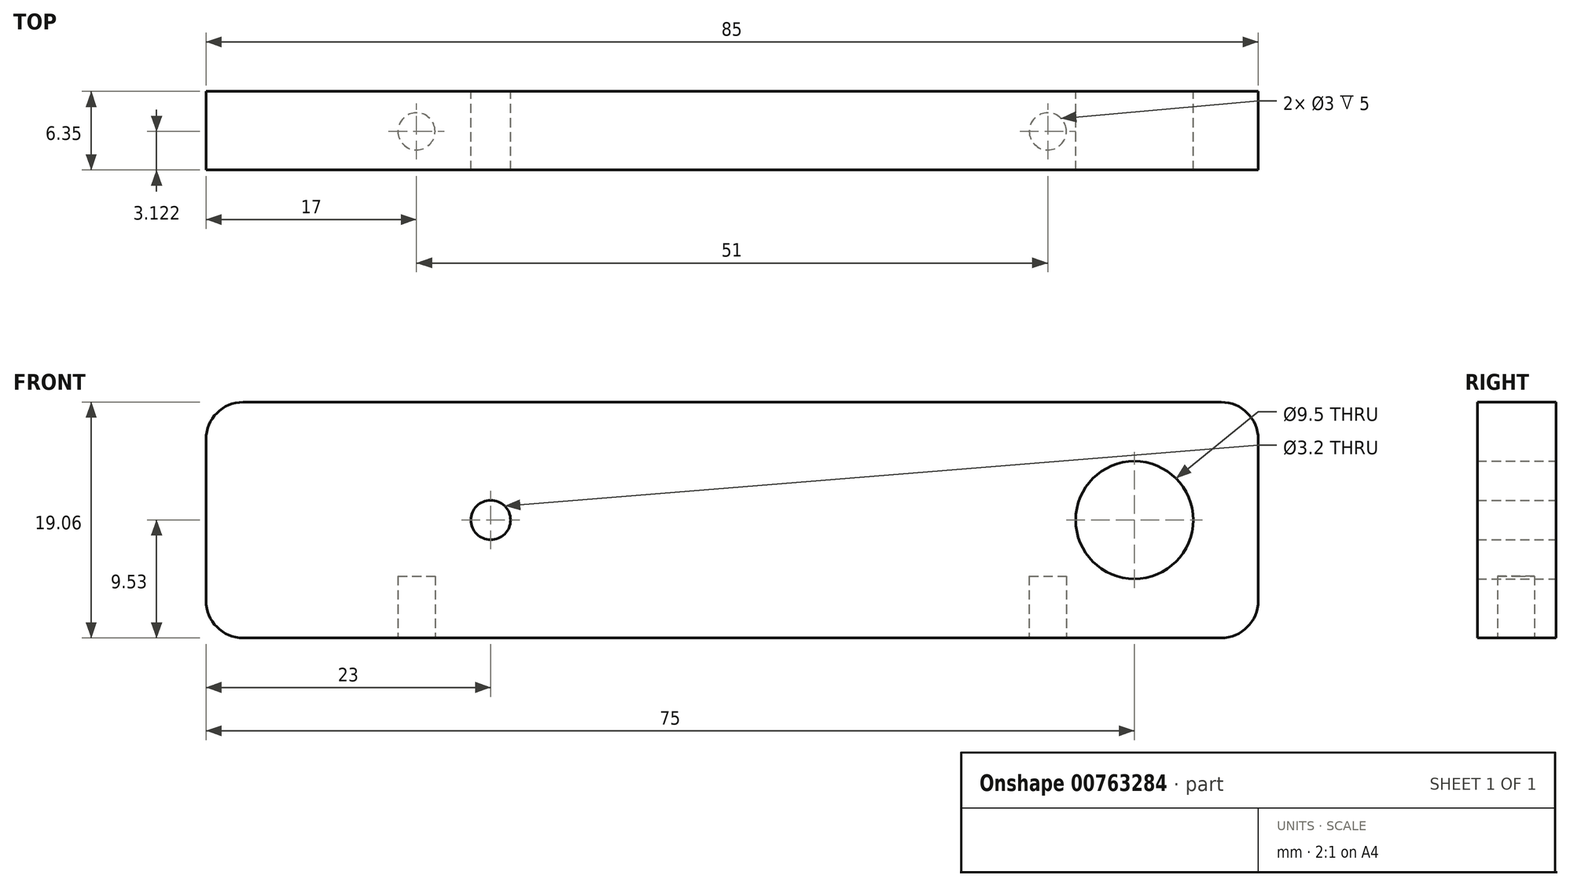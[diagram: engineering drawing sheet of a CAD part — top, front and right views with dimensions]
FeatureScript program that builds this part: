
annotation { "Feature Type Name" : "Feature", "Feature Type Description" : "" }
export const myFeature = defineFeature(function(context is Context, id is Id, definition is map)
    precondition{}
    {
        {
            var Q0;
            Q0=qCreatedBy(makeId("Front.planeOp"),FACE);
            var sketch = newSketch(context, id + "F0", { "sketchPlane" : qUnion([Q0])});
            skLineSegment(sketch, "E0.bottom", {"start": v(-42.5, 9.52) * mm, "end": v(42.5, 9.53) * mm});
            skLineSegment(sketch, "E0.top", {"start": v(-42.5, -9.53) * mm, "end": v(42.5, -9.52) * mm});
            skLineSegment(sketch, "E0.left", {"start": v(-42.5, 9.52) * mm, "end": v(-42.5, -9.53) * mm});
            skLineSegment(sketch, "E0.right", {"start": v(42.5, 9.53) * mm, "end": v(42.5, -9.52) * mm});
            skPoint(sketch, "E0.middle", {"position": v(0, 0) * mm});
            skCircle(sketch, "E1", {"center": v(32.5, 0) * mm, "radius": 4.75 * mm});
            skCircle(sketch, "E2", {"center": v(-19.5, 0) * mm, "radius": 1.6 * mm});
            skSolve(sketch);
        }
        {
            var Q0;
            Q0 = qSketchRegion(id + "F0", true);
            extrude(context, id + "F1", {"entities" : qUnion([Q0]), "depth" : 6.35 * mm, "offsetDistance" : 25 * mm});
        }
        {
            var Q0;
            Q0=makeQuery(id+"F1.opExtrude","SWEPT_EDGE",EDGE,{"disambiguationData":[OSD([sQuery(id+"F0.wireOp",EDGE,"E0.bottom"),sQuery(id+"F0.wireOp",EDGE,"E0.left")])]});
            var Q1;
            Q1=makeQuery(id+"F1.opExtrude","SWEPT_EDGE",EDGE,{"disambiguationData":[OSD([sQuery(id+"F0.wireOp",EDGE,"E0.top"),sQuery(id+"F0.wireOp",EDGE,"E0.left")])]});
            var Q2;
            Q2=makeQuery(id+"F1.opExtrude","SWEPT_EDGE",EDGE,{"disambiguationData":[OSD([sQuery(id+"F0.wireOp",EDGE,"E0.top"),sQuery(id+"F0.wireOp",EDGE,"E0.right")])]});
            var Q3;
            Q3=makeQuery(id+"F1.opExtrude","SWEPT_EDGE",EDGE,{"disambiguationData":[OSD([sQuery(id+"F0.wireOp",EDGE,"E0.bottom"),sQuery(id+"F0.wireOp",EDGE,"E0.right")])]});
            fillet(context, id + "F2", {"entities" : qUnion([Q0, Q1, Q2, Q3]), "radius" : 3 * mm, "tangentPropagation" : true, "allowEdgeOverflow" : false});
        }
        {
            var Q0;
            Q0=makeQuery(id+"F1.opExtrude","SWEPT_FACE",FACE,{"disambiguationData":[OSD([sQuery(id+"F0.wireOp",EDGE,"E0.top")])]});
            var sketch = newSketch(context, id + "F3", { "sketchPlane" : qUnion([Q0])});
            skCircle(sketch, "E3", {"center": v(-25.5, 3.23) * mm, "radius": 1.5 * mm});
            skCircle(sketch, "E4", {"center": v(25.5, 3.23) * mm, "radius": 1.5 * mm});
            skSolve(sketch);
        }
        {
            var Q0;
            Q0 = qSketchRegion(id + "F3", true);
            extrude(context, id + "F4", {"entities" : qUnion([Q0]), "operationType" : NewBodyOperationType.REMOVE, "oppositeDirection" : true, "depth" : 5 * mm, "offsetDistance" : 25 * mm});
        }
    });
